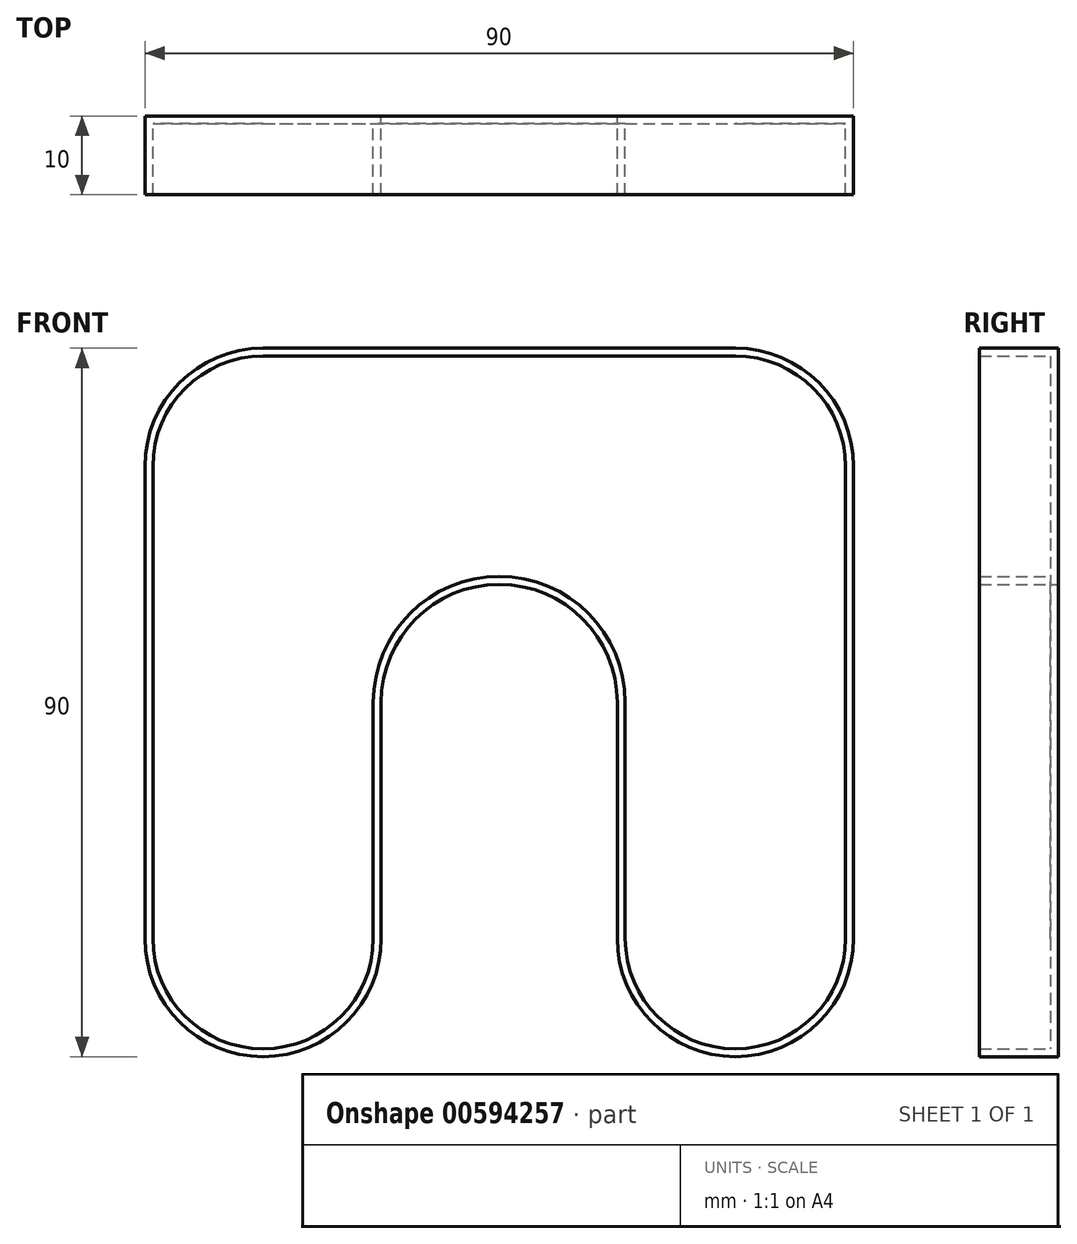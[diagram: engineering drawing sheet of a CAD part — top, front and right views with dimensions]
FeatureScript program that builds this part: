
annotation { "Feature Type Name" : "Feature", "Feature Type Description" : "" }
export const myFeature = defineFeature(function(context is Context, id is Id, definition is map)
    precondition{}
    {
        {
            var Q0;
            Q0=qCreatedBy(makeId("Front.planeOp"),FACE);
            var sketch = newSketch(context, id + "F0", { "sketchPlane" : qUnion([Q0])});
            skLineSegment(sketch, "E0.bottom", {"start": v(-30, 45) * mm, "end": v(30, 45) * mm});
            skLineSegment(sketch, "E0.left", {"start": v(-45, 30) * mm, "end": v(-45, -30) * mm});
            skLineSegment(sketch, "E0.right", {"start": v(45, 30) * mm, "end": v(45, -30) * mm});
            skPoint(sketch, "E0.middle", {"position": v(0, 0) * mm});
            skLineSegment(sketch, "E1.left", {"start": v(-15, -30) * mm, "end": v(-15, 0) * mm});
            skLineSegment(sketch, "E1.right", {"start": v(15, -30) * mm, "end": v(15, 0) * mm});
            skPoint(sketch, "E2.visualSharp", {"position": v(-45, 45) * mm});
            skArc(sketch, "E2.filletArc", {"start": v(-30, 45) * mm, "mid": v(-40.6, 40.6) * mm, "end": v(-45, 30) * mm});
            skPoint(sketch, "E3.visualSharp", {"position": v(45, 45) * mm});
            skArc(sketch, "E3.filletArc", {"start": v(45, 30) * mm, "mid": v(40.6, 40.6) * mm, "end": v(30, 45) * mm});
            skArc(sketch, "E4", {"start": v(-45, -30) * mm, "mid": v(-30, -45) * mm, "end": v(-15, -30) * mm});
            skPoint(sketch, "E4.first.point", {"position": v(-45, -30) * mm});
            skPoint(sketch, "E4.second.point", {"position": v(-30, -45) * mm});
            skPoint(sketch, "E4.third.point", {"position": v(-15, -30) * mm});
            skPoint(sketch, "E5.orphan", {"position": v(-45, -45) * mm});
            skPoint(sketch, "E6.orphan", {"position": v(-15, -45) * mm});
            skArc(sketch, "E7.MirrorCS", {"start": v(45, -30) * mm, "mid": v(30, -45) * mm, "end": v(15, -30) * mm});
            skPoint(sketch, "E8.trimOffspring.end.orphan", {"position": v(45, -45) * mm});
            skArc(sketch, "E9", {"start": v(15, 0) * mm, "mid": v(0, 15) * mm, "end": v(-15, 0) * mm});
            skSolve(sketch);
        }
        {
            var Q0;
            Q0=makeQuery(id+"F0.imprint","IMPRINT",FACE,{"disambiguationData":[TD([[makeQuery(id+"F0.imprint","IMPRINT",EDGE,{"derivedFrom":sQuery(id+"F0.wireOp",EDGE,"E0.bottom")}),-1.0]])]});
            extrude(context, id + "F1", {"entities" : qUnion([Q0]), "depth" : 10 * mm, "offsetDistance" : 25 * mm});
        }
        {
            var Q0;
            Q0=makeQuery(id+"F1.opExtrude","CAP_FACE",FACE,{"disambiguationData":[OSD([sQuery(id+"F0.wireOp",EDGE,"E0.bottom"),sQuery(id+"F0.wireOp",EDGE,"E0.left"),sQuery(id+"F0.wireOp",EDGE,"E0.right"),sQuery(id+"F0.wireOp",EDGE,"E1.left"),sQuery(id+"F0.wireOp",EDGE,"E1.right"),sQuery(id+"F0.wireOp",EDGE,"E2.filletArc"),sQuery(id+"F0.wireOp",EDGE,"E3.filletArc"),sQuery(id+"F0.wireOp",EDGE,"E4"),sQuery(id+"F0.wireOp",EDGE,"E7.MirrorCS"),sQuery(id+"F0.wireOp",EDGE,"E9")])],"isStart":false});
            shell(context, id + "F2", {"entities" : qUnion([Q0]), "thickness" : 1 * mm});
        }
    });
